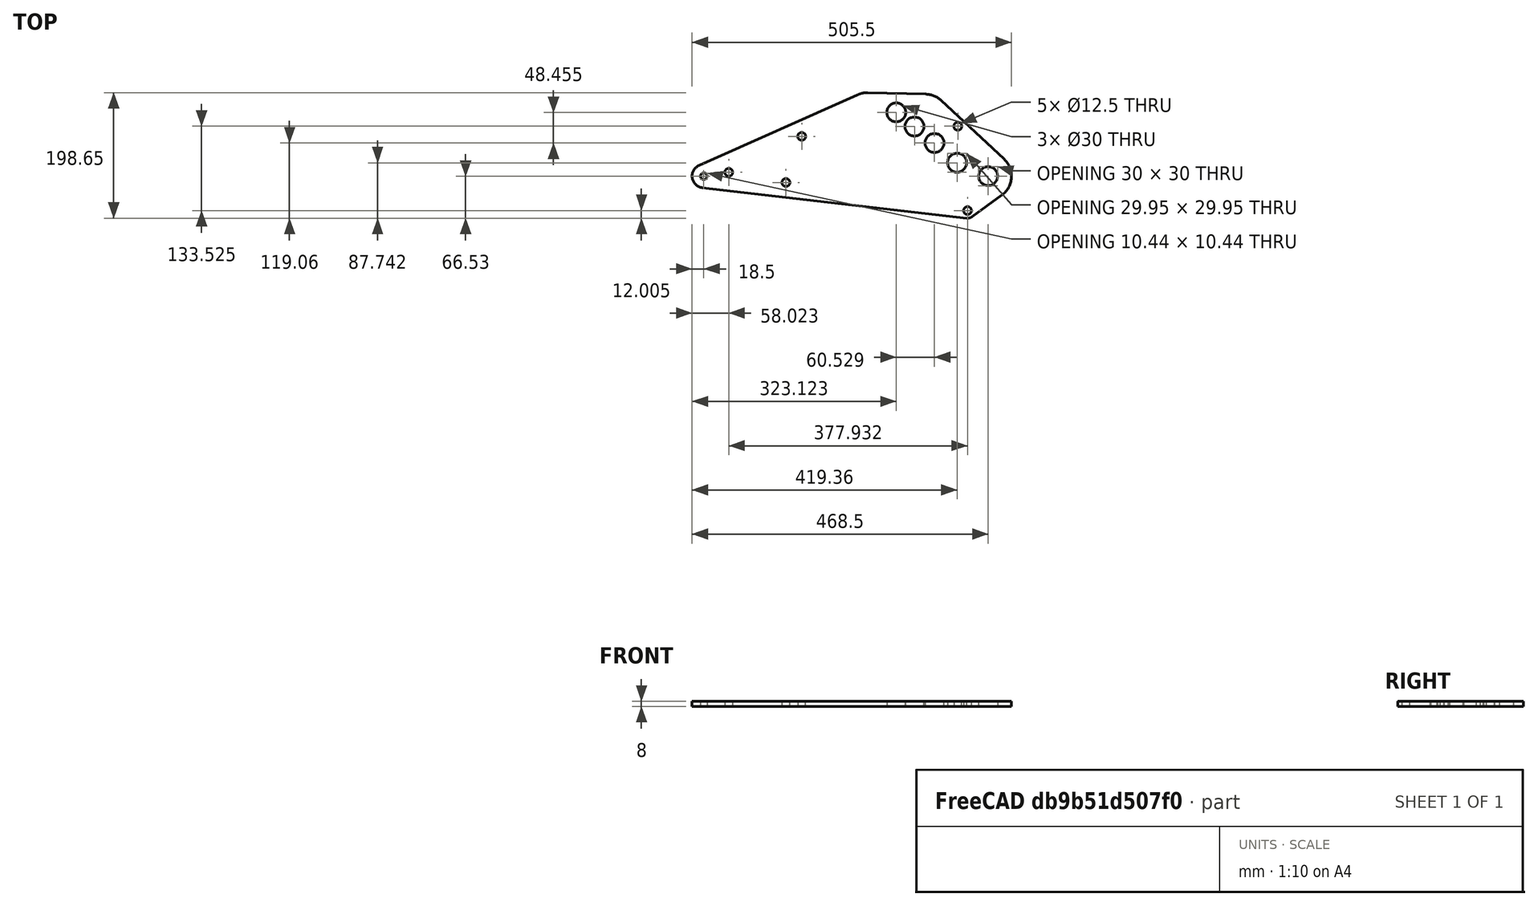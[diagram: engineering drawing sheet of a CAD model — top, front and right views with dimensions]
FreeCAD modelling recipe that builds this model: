
FCSTD DOCUMENT  (FreeCAD 0.19R24267 +99 (Git))
Label: V2 Lever arm FEA_CLEARED
License: All rights reserved
LicenseURL: http://en.wikipedia.org/wiki/All_rights_reserved
objects: Fem::ConstraintForce×2, Sketcher::SketchObject×1, PartDesign::Pad×1, PartDesign::Body×1, Fem::FemSolverObjectPython×1, App::MaterialObjectPython×1, Fem::FemMeshObjectPython×1, Fem::ConstraintFixed×1, Fem::FemAnalysis×1
note: 4 computed .brp shape members not serialized (recipe doc carries the construction recipe); baked Part::Feature solids carry a one-line shape summary decoded from their .brp

FEATURE [Sketcher::SketchObject] Sketch
  FullyConstrained = true
  MapMode = 5
  Support = -> [XY_Plane]
  sketch-geometry (55):
    g0: LineSegment StartX=450 StartY=0 StartZ=0 EndX=160.707 EndY=-670.166 EndZ=0
    g1: Circle CenterX=160.707 CenterY=-670.166 CenterZ=0 NormalX=0 NormalY=0 NormalZ=1 AngleXU=0 Radius=10
    g2: LineSegment StartX=160.707 StartY=-670.166 StartZ=0 EndX=66.2436 EndY=-637.354 EndZ=0
    g3: LineSegment StartX=0 StartY=0 StartZ=0 EndX=5.22187 EndY=0.542737 EndZ=0
    g4: LineSegment StartX=0 StartY=0 StartZ=0 EndX=-5.22187 EndY=-0.542737 EndZ=0
    g5: ArcOfCircle CenterX=0 CenterY=0 CenterZ=0 NormalX=0 NormalY=0 NormalZ=1 AngleXU=0 Radius=5.25 StartAngle=0.103564 EndAngle=3.24516
    g6: ArcOfCircle CenterX=0 CenterY=0 CenterZ=0 NormalX=0 NormalY=0 NormalZ=1 AngleXU=0 Radius=5.25 StartAngle=3.24516 EndAngle=6.38675
    g7: LineSegment StartX=0 StartY=0 StartZ=0 EndX=66.2436 EndY=-637.354 EndZ=0
    g8: LineSegment StartX=463.772 StartY=-5.94486 StartZ=0 EndX=450 EndY=0 EndZ=0
    g9: LineSegment StartX=450 StartY=0 StartZ=0 EndX=436.228 EndY=5.94486 EndZ=0
    g10: ArcOfCircle CenterX=450 CenterY=0 CenterZ=0 NormalX=0 NormalY=0 NormalZ=1 AngleXU=0 Radius=15 StartAngle=5.87568 EndAngle=9.01727
    g11: ArcOfCircle CenterX=450 CenterY=0 CenterZ=0 NormalX=0 NormalY=0 NormalZ=1 AngleXU=0 Radius=15 StartAngle=2.73408 EndAngle=5.87568
    g12: LineSegment StartX=386.691 StartY=26.1342 StartZ=0 EndX=400.86 EndY=21.2124 EndZ=0
    g13: LineSegment StartX=400.86 StartY=21.2124 StartZ=0 EndX=415.03 EndY=16.2905 EndZ=0
    g14: ArcOfCircle CenterX=400.86 CenterY=21.2124 CenterZ=0 NormalX=0 NormalY=0 NormalZ=1 AngleXU=0 Radius=15 StartAngle=5.94887 EndAngle=9.09046
    g15: ArcOfCircle CenterX=400.86 CenterY=21.2124 CenterZ=0 NormalX=0 NormalY=0 NormalZ=1 AngleXU=0 Radius=15 StartAngle=2.80728 EndAngle=5.94887
    g16: LineSegment StartX=0 StartY=0 StartZ=0 EndX=400.86 EndY=21.2124 EndZ=0
    g17: LineSegment StartX=400.86 StartY=21.2124 StartZ=0 EndX=450 EndY=0 EndZ=0
    g18: LineSegment StartX=450 StartY=0 StartZ=0 EndX=333.422 EndY=78.6058 EndZ=0
    g19: LineSegment StartX=333.422 StartY=78.6058 StartZ=0 EndX=0 EndY=0 EndZ=0
    g20: LineSegment StartX=0 StartY=0 StartZ=0 EndX=304.623 EndY=100.985 EndZ=0
    g21: LineSegment StartX=304.623 StartY=100.985 StartZ=0 EndX=450 EndY=0 EndZ=0
    g22: LineSegment StartX=450 StartY=0 StartZ=0 EndX=365.152 EndY=52.53 EndZ=0
    g23: LineSegment StartX=365.152 StartY=52.53 StartZ=0 EndX=0 EndY=0 EndZ=0
    g24: Circle CenterX=304.623 CenterY=100.985 CenterZ=0 NormalX=0 NormalY=0 NormalZ=1 AngleXU=0 Radius=15
    g25: Circle CenterX=365.152 CenterY=52.53 CenterZ=0 NormalX=0 NormalY=0 NormalZ=1 AngleXU=0 Radius=15
    g26: Circle CenterX=333.422 CenterY=78.6058 CenterZ=0 NormalX=0 NormalY=0 NormalZ=1 AngleXU=0 Radius=15
    g27: ArcOfCircle CenterX=0 CenterY=0 CenterZ=0 NormalX=0 NormalY=0 NormalZ=1 AngleXU=0 Radius=18.5 StartAngle=1.99078 EndAngle=4.59795
    g28: LineSegment StartX=0 StartY=0 StartZ=0 EndX=417.454 EndY=-54.5254 EndZ=0
    g29: LineSegment StartX=417.454 StartY=-54.5254 StartZ=0 EndX=450 EndY=0 EndZ=0
    g30: ArcOfCircle CenterX=417.454 CenterY=-54.5254 CenterZ=0 NormalX=0 NormalY=0 NormalZ=1 AngleXU=0 Radius=12 StartAngle=4.59795 EndAngle=5.3404
    g31: ArcOfCircle CenterX=450 CenterY=0 CenterZ=0 NormalX=0 NormalY=0 NormalZ=1 AngleXU=0 Radius=37 StartAngle=5.3404 EndAngle=7.10303
    g32: LineSegment StartX=-2.1125 StartY=-18.379 StartZ=0 EndX=416.084 EndY=-66.4469 EndZ=0
    g33: LineSegment StartX=424.505 StartY=-64.2358 StartZ=0 EndX=471.739 EndY=-29.9403 EndZ=0
    g34: Circle CenterX=417.454 CenterY=-54.5254 CenterZ=0 NormalX=0 NormalY=0 NormalZ=1 AngleXU=0 Radius=6.25
    g35: Circle CenterX=130 CenterY=-10 CenterZ=0 NormalX=0 NormalY=0 NormalZ=1 AngleXU=0 Radius=6.25
    g36: Circle CenterX=155 CenterY=63 CenterZ=0 NormalX=0 NormalY=0 NormalZ=1 AngleXU=0 Radius=6.25
    g37: Circle CenterX=39.5227 CenterY=6.16105 CenterZ=0 NormalX=0 NormalY=0 NormalZ=1 AngleXU=0 Radius=6.25
    g38: LineSegment StartX=0 StartY=0 StartZ=0 EndX=130 EndY=-10 EndZ=0
    g39: LineSegment StartX=155 StartY=63 StartZ=0 EndX=0 EndY=0 EndZ=0
    g40: Circle CenterX=39.5227 CenterY=6.16105 CenterZ=0 NormalX=0 NormalY=0 NormalZ=1 AngleXU=0 Radius=9.17415
    g41: Circle CenterX=402 CenterY=79 CenterZ=0 NormalX=0 NormalY=0 NormalZ=1 AngleXU=0 Radius=6.25
    g42: Circle CenterX=402 CenterY=79 CenterZ=0 NormalX=0 NormalY=0 NormalZ=1 AngleXU=0 Radius=12
    g43: LineSegment StartX=243.297 StartY=128.904 StartZ=0 EndX=-7.54323 EndY=16.8923 EndZ=0
    g44: LineSegment StartX=259.293 StartY=132.109 StartZ=0 EndX=351.428 EndY=129.843 EndZ=0
    g45: LineSegment StartX=304.623 StartY=100.985 StartZ=0 EndX=305.36 EndY=130.976 EndZ=0
    g46: ArcOfCircle CenterX=258.383 CenterY=95.1197 CenterZ=0 NormalX=0 NormalY=0 NormalZ=1 AngleXU=0 Radius=37 StartAngle=1.54621 EndAngle=1.99078
    g47: ArcOfCircle CenterX=350.518 CenterY=92.8542 CenterZ=0 NormalX=0 NormalY=0 NormalZ=1 AngleXU=0 Radius=37 StartAngle=0.819844 EndAngle=1.54621
    g48: LineSegment StartX=400.86 StartY=21.2124 StartZ=0 EndX=160.707 EndY=-670.166 EndZ=0
    g49: LineSegment StartX=375.764 StartY=119.903 StartZ=0 EndX=475.246 EndY=27.0485 EndZ=0
    g50: Circle CenterX=450 CenterY=0 CenterZ=0 NormalX=0 NormalY=0 NormalZ=1 AngleXU=0 Radius=6.5
    g51: Circle CenterX=400.86 CenterY=21.2124 CenterZ=0 NormalX=0 NormalY=0 NormalZ=1 AngleXU=0 Radius=6.5
    g52: Circle CenterX=365.152 CenterY=52.53 CenterZ=0 NormalX=0 NormalY=0 NormalZ=1 AngleXU=0 Radius=6.5
    g53: Circle CenterX=333.422 CenterY=78.6058 CenterZ=0 NormalX=0 NormalY=0 NormalZ=1 AngleXU=0 Radius=6.5
    g54: Circle CenterX=304.623 CenterY=100.985 CenterZ=0 NormalX=0 NormalY=0 NormalZ=1 AngleXU=0 Radius=6.5
  constraints (143):
    c: Coincident(g2,g1)
    c: Distance(g2) = 100
    c: Coincident(g4,g3)
    c: Parallel(g4,g3)
    c: Coincident(g5,g3)
    c: Coincident(g5,g4)
    c: Coincident(g5,g3)
    c: Coincident(g6,g3)
    c: Coincident(g6,g4)
    c: Coincident(g6,g3)
    c: Coincident(g7,g3)
    c: Perpendicular(g7,g3)
    c: Coincident(g3,g-1)
    c: Coincident(g7,g2)
    c: Coincident(g9,g8)
    c: Parallel(g9,g8)
    c: Coincident(g10,g8)
    c: Coincident(g10,g9)
    c: Coincident(g10,g8)
    c: Coincident(g11,g8)
    c: Coincident(g11,g8)
    c: Coincident(g11,g9)
    c: Coincident(g8,g0)
    c: Perpendicular(g8,g0)
    c: PointOnObject(g0,g-1)
    c: Coincident(g13,g12)
    c: Parallel(g12,g13)
    c: Coincident(g14,g12)
    c: Coincident(g14,g12)
    c: Coincident(g14,g13)
    c: Coincident(g15,g12)
    c: Coincident(g15,g13)
    c: Coincident(g15,g12)
    c: Coincident(g16,g5)
    c: Coincident(g16,g14)
    c: Coincident(g17,g14)
    c: Coincident(g17,g10)
    c: Coincident(g18,g10)
    c: Coincident(g19,g18)
    c: Coincident(g19,g5)
    c: Coincident(g20,g5)
    c: Coincident(g21,g20)
    c: Coincident(g21,g10)
    c: Coincident(g22,g10)
    c: Coincident(g23,g22)
    c: Coincident(g23,g5)
    c: DistanceX(g5,g10) = 450
    c: Coincident(g24,g20)
    c: Coincident(g25,g22)
    c: Coincident(g26,g18)
    c: Equal(g10,g14)
    c: Equal(g14,g26)
    c: Equal(g26,g25)
    c: Equal(g25,g24)
    c: Distance(g16) = 401.421
    c: Distance(g19) = 342.563
    c: Distance(g23) = 368.911
    c: Distance(g20) = 320.925
    c: Distance(g21) = 177.01
    c: Distance(g22) = 99.7928
    c: Distance(g18) = 140.603
    c: Distance(g17) = 53.5228
    c: Radius(g1) = 10
    c: Perpendicular(g0,g17)
    c: Distance(g7) = 640.787
    c: DistanceY(g-1,g14) = 21.2124
    c: DistanceY(g-1,g25) = 52.53
    c: DistanceY(g-1,g26) = 78.6058
    c: DistanceY(g-1,g24) = 100.985
    c: Angle(g0,g7) = 0.511073
    c: Coincident(g27,g5)
    c: Coincident(g28,g5)
    c: Coincident(g29,g28)
    c: Coincident(g29,g10)
    c: Distance(g28) = 421
    c: Distance(g29) = 63.5
    c: Coincident(g30,g28)
    c: Coincident(g31,g10)
    c: Tangent(g27,g32) = -1.5708
    c: Tangent(g30,g32) = -1.5708
    c: Tangent(g30,g33) = -1.5708
    c: Tangent(g31,g33) = -1.5708
    c: Radius(g31) = 37
    c: Radius(g27) = 18.5
    c: Coincident(g34,g30)
    c: DistanceY(g35,g-1) = 10
    c: DistanceX(g-1,g35) = 130
    c: DistanceX(g-1,g36) = 155
    c: DistanceY(g-1,g36) = 63
    c: Radius(g30) = 12
    c: Equal(g34,g35)
    c: Equal(g35,g36)
    c: Equal(g36,g37)
    c: Coincident(g38,g5)
    c: Coincident(g38,g35)
    c: Coincident(g39,g36)
    c: Coincident(g39,g5)
    c: Tangent(g40,g39)
    c: Tangent(g40,g38)
    c: Coincident(g40,g37)
    c: Distance(g5,g37) = 40
    c: Equal(g41,g37)
    c: DistanceX(g41) = 402
    c: DistanceY(g-1,g41) = 79
    c: Coincident(g42,g41)
    c: Radius(g42) = 12
    c: Tangent(g43,g27) = -1.5708
    c: Angle(g17,g44) = 0.382925
    c: Coincident(g45,g24)
    c: PointOnObject(g45,g44)
    c: Distance(g45) = 30
    c: Tangent(g44,g46) = 1.5708
    c: Tangent(g43,g46) = -1.5708
    c: Tangent(g44,g47) = 1.5708
    c: Symmetric(g44,g44,g45)
    c: Equal(g31,g47)
    c: Equal(g47,g46)
    c: Coincident(g48,g14)
    c: Coincident(g48,g0)
    c: Perpendicular(g48,g13)
    c: Distance(g48) = 731.9
    c: Perpendicular(g2,g48)
    c: Coincident(g0,g1)
    c: Tangent(g49,g31) = 1.5708
    c: Tangent(g49,g47) = 1.5708
    c: Tangent(g42,g49)
    c: Diameter(g5) = 10.5
    c: Diameter(g37) = 12.5
    c: Diameter(g10) = 30
    c: Angle(g0,g48) = 0.0731939
    c: Angle(g48,g7) = 0.437879
    c: Angle(g7,g16) = 1.5201
    c: Angle(g17,g0) = 1.5708
    c: Coincident(g50,g10)
    c: Coincident(g51,g14)
    c: Coincident(g52,g25)
    c: Coincident(g53,g26)
    c: Coincident(g54,g24)
    c: Diameter(g50) = 13
    c: Equal(g50,g51)
    c: Equal(g51,g52)
    c: Equal(g52,g53)
    c: Equal(g53,g54)
FEATURE [PartDesign::Pad] Pad
  Direction = (1,1,1)
  Length = 8
  Length2 = 100
  Profile = -> Sketch
  Type = 0
FEATURE [PartDesign::Body] Body
  Group = -> [Sketch,Pad]
  Origin = -> Origin
  Tip = -> Pad
FEATURE [Fem::FemSolverObjectPython] SolverCcxTools  # FEM object (typed FeaturePython)
  AnalysisType = 0
  BeamShellResultOutput3D = false
  EigenmodeHighLimit = 1000000
  EigenmodeLowLimit = 0
  EigenmodesCount = 10
  GeometricalNonlinearity = 0
  IterationsControlParameterCutb = 0.25,0.5,0.75,0.85,,,1.5,
  IterationsControlParameterIter = 4,8,9,200,10,400,,200,,
  IterationsControlParameterTimeUse = false
  IterationsThermoMechMaximum = 2000
  IterationsUserDefinedIncrementations = false
  IterationsUserDefinedTimeStepLength = false
  MaterialNonlinearity = 0
  MatrixSolverType = 0
  SplitInputWriter = false
  ThermoMechSteadyState = true
  TimeEnd = 1
  TimeInitialStep = 0.01
FEATURE [App::MaterialObjectPython] MaterialSolid  # material (typed FeaturePython)
  Category = 0
  Material = AuthorAndLicense=CalculiX-Steel,CardName=CalculiX-Steel,Density=7900 kg/m^3,Description=Standard steel material for CalculiX sample calculations,+7 more (map truncated)
FEATURE [Fem::FemMeshObjectPython] FEMMeshGmsh  # FEM object (typed FeaturePython)
  Algorithm2D = 0
  Algorithm3D = 0
  CharacteristicLengthMax = 3
  CharacteristicLengthMin = 0
  CoherenceMesh = true
  ElementDimension = 0
  ElementOrder = 1
  GeometryTolerance = 1e-06
  GroupsOfNodes = false
  HighOrderOptimize = false
  OptimizeNetgen = false
  OptimizeStd = true
  Part = -> Pad
  RecombineAll = false
  SecondOrderLinear = false
FEATURE [Fem::ConstraintFixed] ConstraintFixed
  NormalDirection = (0.103379,-0.994642,0)
  Normals = (18) [(-0.994642,-0.103379,0),(0.103379,-0.994642,0),(0.994642,0.103379,0),(-0.994642,-0.103379,0),(0.103379,-0.994642,0),(0.994642,0.103379,0),+12 more]
  Points = (18) [(5.22187,0.542737,8),(-0.542737,5.22187,8),(-5.22187,-0.542737,8),(5.22187,0.542737,4),(-0.542737,5.22187,4),(-5.22187,-0.542737,4),+12 more]
  References = -> [Pad]
FEATURE [Fem::ConstraintForce] ConstraintForce001
  DirectionVector = (0.396324,0.918111,0)
  Force = 11596.5
  NormalDirection = (-0.396324,-0.918111,0)
  Points = (12) [(463.772,-5.94486,8),(462.034,8.95418,8),(448.263,14.899,8),(436.228,5.94486,8),(463.772,-5.94486,4),(462.034,8.95418,4),(448.263,14.899,4),+5 more]
  References = -> [Pad]
  Reversed = true
  Scale = 4
FEATURE [Fem::ConstraintForce] ConstraintForce002
  DirectionVector = (-0.328123,-0.944635,0)
  Force = 13376.8
  NormalDirection = (0.328123,0.944635,0)
  Points = (12) [(386.691,26.1342,8),(389.513,11.4021,8),(403.682,6.48028,8),(415.03,16.2905,8),(386.691,26.1342,4),(389.513,11.4021,4),(403.682,6.48028,4),+5 more]
  References = -> [Pad]
  Reversed = true
  Scale = 4
FEATURE [Fem::FemAnalysis] Analysis
  Group = -> [SolverCcxTools,MaterialSolid,FEMMeshGmsh,ConstraintFixed,ConstraintForce001,ConstraintForce002]
